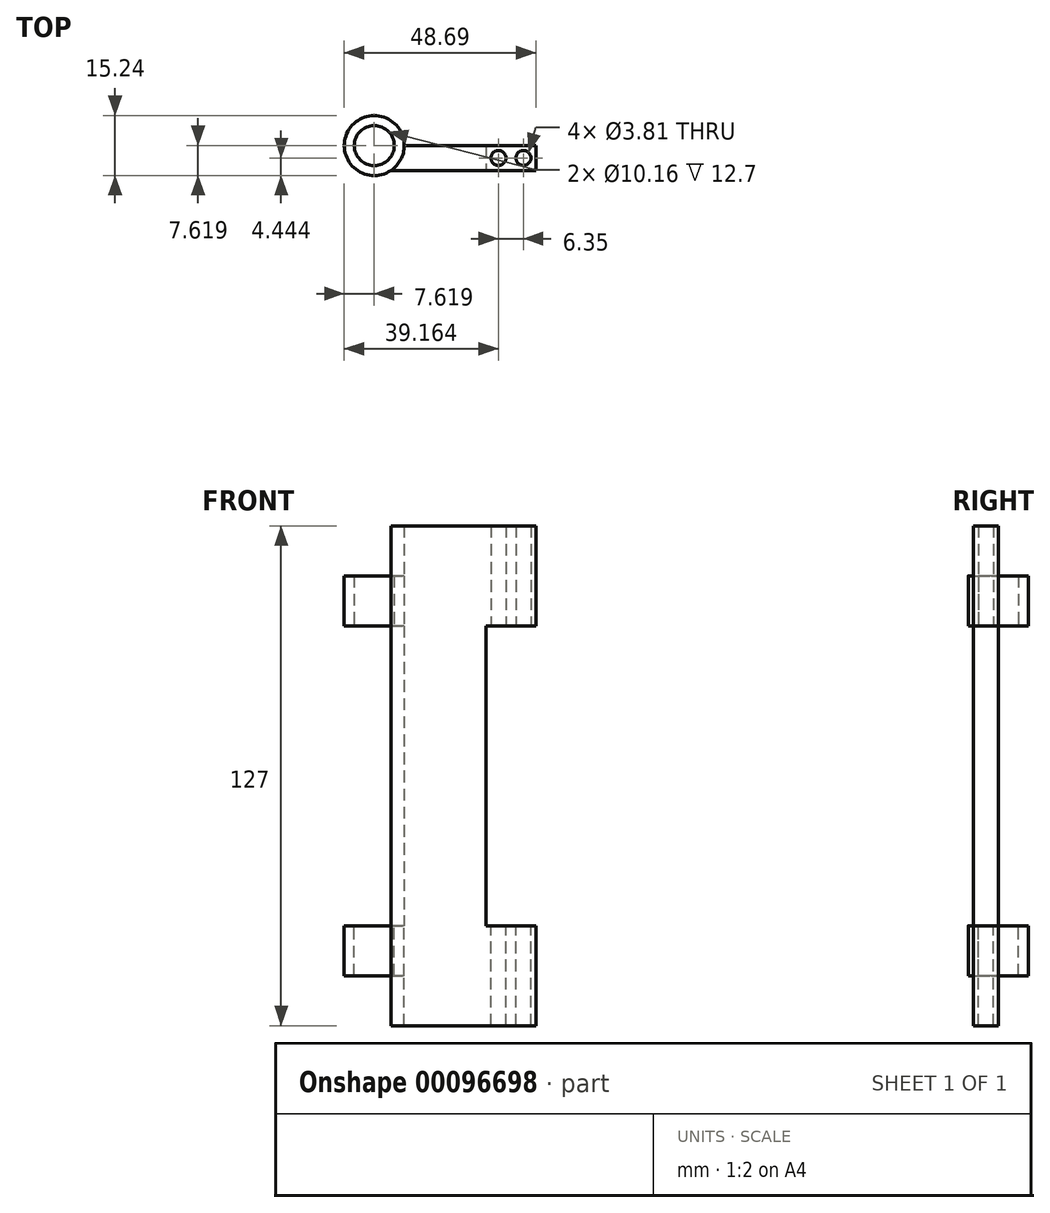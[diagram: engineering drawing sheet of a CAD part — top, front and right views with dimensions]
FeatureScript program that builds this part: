
annotation { "Feature Type Name" : "Feature", "Feature Type Description" : "" }
export const myFeature = defineFeature(function(context is Context, id is Id, definition is map)
    precondition{}
    {
        {
            var Q0;
            Q0=qCreatedBy(makeId("Top.planeOp"),FACE);
            var sketch = newSketch(context, id + "F0", { "sketchPlane" : qUnion([Q0])});
            skLineSegment(sketch, "E0", {"start": v(-20.3, -33.32) * mm, "end": v(-33, -33.32) * mm});
            skLineSegment(sketch, "E1", {"start": v(-20.3, -26.97) * mm, "end": v(-61.36, -26.97) * mm});
            skLineSegment(sketch, "E2.MirrorCS", {"start": v(-20.3, -20.62) * mm, "end": v(-33, -20.62) * mm});
            skCircle(sketch, "E3", {"center": v(-61.36, -26.97) * mm, "radius": 7.62 * mm});
            skLineSegment(sketch, "E4", {"start": v(-20.3, -20.62) * mm, "end": v(-20.3, -26.97) * mm});
            skLineSegment(sketch, "E5", {"start": v(-20.3, -26.97) * mm, "end": v(-20.3, -33.32) * mm});
            skCircle(sketch, "E6", {"center": v(-61.36, -26.97) * mm, "radius": 5.08 * mm});
            skLineSegment(sketch, "E7", {"start": v(-33, -20.62) * mm, "end": v(-57.15, -20.62) * mm});
            skLineSegment(sketch, "E8", {"start": v(-33, -33.32) * mm, "end": v(-57.15, -33.32) * mm});
            skLineSegment(sketch, "E9", {"start": v(-33, -20.62) * mm, "end": v(-33, -26.97) * mm});
            skLineSegment(sketch, "E10", {"start": v(-33, -26.97) * mm, "end": v(-33, -33.32) * mm});
            skCircle(sketch, "E11", {"center": v(-29.82, -23.8) * mm, "radius": 1.9 * mm});
            skCircle(sketch, "E12.MirrorC", {"center": v(-23.47, -23.8) * mm, "radius": 1.9 * mm});
            skCircle(sketch, "E13.MirrorC", {"center": v(-29.82, -30.15) * mm, "radius": 1.9 * mm});
            skCircle(sketch, "E14.MirrorC", {"center": v(-23.47, -30.15) * mm, "radius": 1.9 * mm});
            skLineSegment(sketch, "E15", {"start": v(-26.64, -20.62) * mm, "end": v(-26.64, -26.97) * mm});
            skLineSegment(sketch, "E16", {"start": v(-26.64, -26.97) * mm, "end": v(-26.64, -33.32) * mm});
            skSolve(sketch);
        }
        {
            var Q0;
            {var subQ4=sQuery(id+"F0.wireOp",EDGE,"E8");Q0=makeQuery(id+"F0.imprint","IMPRINT",FACE,{"disambiguationData":[TD([[makeQuery(id+"F0.imprint","IMPRINT",EDGE,{"derivedFrom":subQ4}),-1.0]])]});}
            var Q1;
            {var subQ0=sQuery(id+"F0.wireOp",EDGE,"E10");Q1=makeQuery(id+"F0.imprint","IMPRINT",FACE,{"disambiguationData":[TD([[makeQuery(id+"F0.imprint","IMPRINT",EDGE,{"derivedFrom":subQ0}),1.0]])]});}
            var Q2;
            {var subQ0=sQuery(id+"F0.wireOp",EDGE,"E5");Q2=makeQuery(id+"F0.imprint","IMPRINT",FACE,{"disambiguationData":[TD([[makeQuery(id+"F0.imprint","IMPRINT",EDGE,{"derivedFrom":subQ0}),-1.0]])]});}
            extrude(context, id + "F1", {"entities" : qUnion([Q0, Q1, Q2]), "oppositeDirection" : true, "depth" : 25.4 * mm});
        }
        {
            var Q0;
            Q0=makeQuery(id+"F0.imprint","IMPRINT",FACE,{"disambiguationData":[TD([[makeQuery(id+"F0.imprint","IMPRINT",EDGE,{"derivedFrom":sQuery(id+"F0.wireOp",EDGE,"E6")}),-1.0]])]});
            extrude(context, id + "F2", {"entities" : qUnion([Q0]), "operationType" : NewBodyOperationType.ADD, "oppositeDirection" : true, "depth" : 12.7 * mm});
        }
        {
            var Q0;
            {var subQ4=sQuery(id+"F0.wireOp",EDGE,"E8");Q0=makeQuery(id+"F0.imprint","IMPRINT",FACE,{"disambiguationData":[TD([[makeQuery(id+"F0.imprint","IMPRINT",EDGE,{"derivedFrom":subQ4}),-1.0]])]});}
            extrude(context, id + "F3", {"entities" : qUnion([Q0]), "operationType" : NewBodyOperationType.ADD, "depth" : 38.1 * mm});
        }
        {
            var Q0;
            Q0=makeQuery(id+"F1.opExtrude","SWEPT_BODY",BODY,{"disambiguationData":[OSD([sQuery(id+"F0.wireOp",EDGE,"E0"),sQuery(id+"F0.wireOp",EDGE,"E1"),sQuery(id+"F0.wireOp",EDGE,"E3"),sQuery(id+"F0.wireOp",EDGE,"E5"),sQuery(id+"F0.wireOp",EDGE,"E8"),sQuery(id+"F0.wireOp",EDGE,"E13.MirrorC"),sQuery(id+"F0.wireOp",EDGE,"E14.MirrorC")])]});
            var Q1;
            Q1=makeQuery(id+"F3.opExtrude","CAP_FACE",FACE,{"disambiguationData":[OSD([sQuery(id+"F0.wireOp",EDGE,"E1"),sQuery(id+"F0.wireOp",EDGE,"E3"),sQuery(id+"F0.wireOp",EDGE,"E8"),sQuery(id+"F0.wireOp",EDGE,"E10")])],"isStart":false});
            mirror(context, id + "F4", {"operationType" : NewBodyOperationType.ADD, "entities" : qUnion([Q0]), "mirrorPlane" : qUnion([Q1])});
        }
    });
